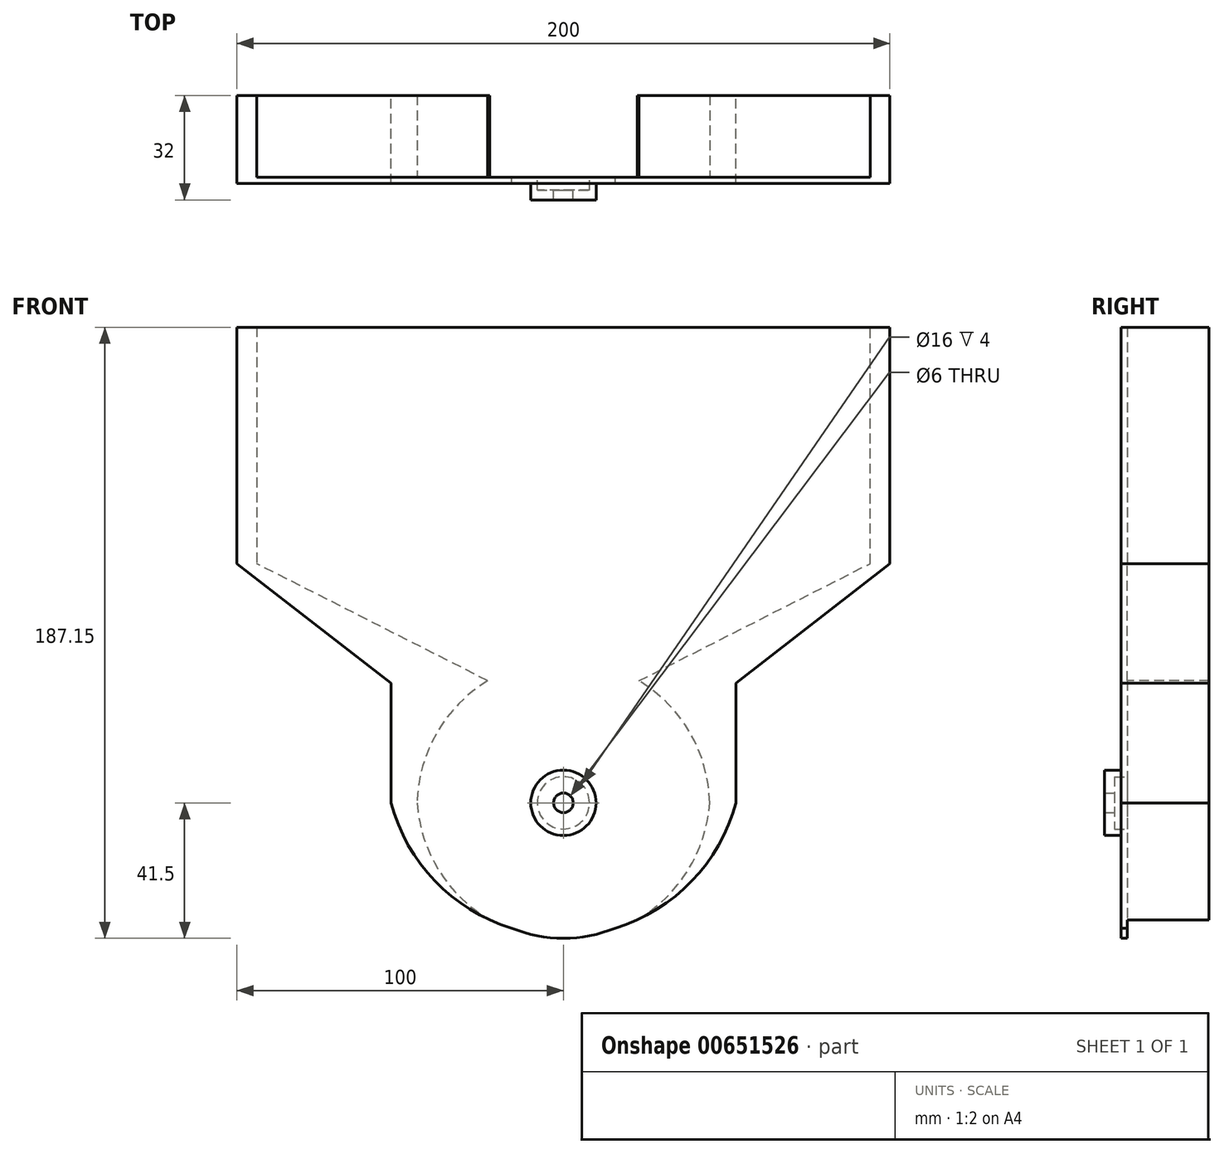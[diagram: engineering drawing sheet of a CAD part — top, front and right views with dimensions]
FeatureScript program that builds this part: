
annotation { "Feature Type Name" : "Feature", "Feature Type Description" : "" }
export const myFeature = defineFeature(function(context is Context, id is Id, definition is map)
    precondition{}
    {
        {
            var Q0;
            Q0=qCreatedBy(makeId("Front.planeOp"),FACE);
            var sketch = newSketch(context, id + "F0", { "sketchPlane" : qUnion([Q0])});
            skArc(sketch, "E0", {"start": v(15.88, -38.34) * mm, "mid": v(41.5, 0) * mm, "end": v(15.88, 38.34) * mm});
            skLineSegment(sketch, "E1", {"start": v(0, 0) * mm, "end": v(0, -41.5) * mm});
            skLineSegment(sketch, "E2", {"start": v(0, 0) * mm, "end": v(-15.88, -38.34) * mm});
            skLineSegment(sketch, "E3", {"start": v(0, 0) * mm, "end": v(15.88, -38.34) * mm});
            skArc(sketch, "E4", {"start": v(-15.88, -38.34) * mm, "mid": v(-39.33, -23.97) * mm, "end": v(-52.8, 0) * mm});
            skArc(sketch, "E5", {"start": v(15.88, -38.34) * mm, "mid": v(39.33, -23.97) * mm, "end": v(52.8, 0) * mm});
            skLineSegment(sketch, "E6", {"start": v(0, 0) * mm, "end": v(-15.88, 38.34) * mm});
            skLineSegment(sketch, "E7", {"start": v(0, 0) * mm, "end": v(15.88, 38.34) * mm});
            skArc(sketch, "E8.trimOffspring", {"start": v(-15.88, 38.34) * mm, "mid": v(-41.5, 0) * mm, "end": v(-15.88, -38.34) * mm});
            skArc(sketch, "E9", {"start": v(-15.88, -38.34) * mm, "mid": v(0, -41.5) * mm, "end": v(15.88, -38.34) * mm});
            skArc(sketch, "E10", {"start": v(-15.88, 38.34) * mm, "mid": v(0, 41.5) * mm, "end": v(15.88, 38.34) * mm});
            skLineSegment(sketch, "E11", {"start": v(-52.8, 0) * mm, "end": v(-52.8, 36.63) * mm});
            skLineSegment(sketch, "E12", {"start": v(-52.8, 36.63) * mm, "end": v(-100, 73.29) * mm});
            skLineSegment(sketch, "E13", {"start": v(-100, 73.29) * mm, "end": v(-100, 145.65) * mm});
            skLineSegment(sketch, "E14", {"start": v(0, 145.65) * mm, "end": v(-100, 145.65) * mm});
            skPoint(sketch, "E14.startSnap0", {"position": v(0, 41.5) * mm});
            skLineSegment(sketch, "E15", {"start": v(0, 145.65) * mm, "end": v(100, 145.65) * mm});
            skLineSegment(sketch, "E16", {"start": v(100, 145.65) * mm, "end": v(100, 73.29) * mm});
            skLineSegment(sketch, "E17", {"start": v(52.8, 0) * mm, "end": v(52.8, 36.63) * mm});
            skLineSegment(sketch, "E18", {"start": v(52.8, 36.63) * mm, "end": v(100, 73.29) * mm});
            skSolve(sketch);
        }
        {
            var Q0;
            Q0 = qSketchRegion(id + "F0", true);
            var Q1;
            Q1=makeQuery(id+"F0.imprint","IMPRINT",FACE,{"disambiguationData":[TD([[makeQuery(id+"F0.imprint","IMPRINT",EDGE,{"derivedFrom":sQuery(id+"F0.wireOp",EDGE,"E6")}),-1.0]])]});
            extrude(context, id + "F1", {"entities" : qUnion([Q0, Q1]), "depth" : 2 * mm, "offsetDistance" : 25 * mm});
        }
        {
            var Q0;
            Q0=makeQuery(id+"F1.opExtrude","CAP_FACE",FACE,{"disambiguationData":[OSD([sQuery(id+"F0.wireOp",EDGE,"E4"),sQuery(id+"F0.wireOp",EDGE,"E5"),sQuery(id+"F0.wireOp",EDGE,"E9"),sQuery(id+"F0.wireOp",EDGE,"E11"),sQuery(id+"F0.wireOp",EDGE,"E12"),sQuery(id+"F0.wireOp",EDGE,"E13"),sQuery(id+"F0.wireOp",EDGE,"E14"),sQuery(id+"F0.wireOp",EDGE,"E15"),sQuery(id+"F0.wireOp",EDGE,"E16"),sQuery(id+"F0.wireOp",EDGE,"E17"),sQuery(id+"F0.wireOp",EDGE,"E18")])],"isStart":false});
            var sketch = newSketch(context, id + "F2", { "sketchPlane" : qUnion([Q0])});
            skCircle(sketch, "E19", {"center": v(0, 0) * mm, "radius": 10 * mm});
            skSolve(sketch);
        }
        {
            var Q0;
            Q0=makeQuery(id+"F2.imprint","IMPRINT",FACE,{"disambiguationData":[TD([[makeQuery(id+"F2.imprint","IMPRINT",EDGE,{"derivedFrom":sQuery(id+"F2.wireOp",EDGE,"E19")}),1.0]])]});
            extrude(context, id + "F3", {"entities" : qUnion([Q0]), "operationType" : NewBodyOperationType.ADD, "depth" : 5 * mm, "offsetDistance" : 25 * mm});
        }
        {
            var Q0;
            Q0=makeQuery(id+"F1.opExtrude","CAP_FACE",FACE,{"disambiguationData":[OSD([sQuery(id+"F0.wireOp",EDGE,"E4"),sQuery(id+"F0.wireOp",EDGE,"E5"),sQuery(id+"F0.wireOp",EDGE,"E9"),sQuery(id+"F0.wireOp",EDGE,"E11"),sQuery(id+"F0.wireOp",EDGE,"E12"),sQuery(id+"F0.wireOp",EDGE,"E13"),sQuery(id+"F0.wireOp",EDGE,"E14"),sQuery(id+"F0.wireOp",EDGE,"E15"),sQuery(id+"F0.wireOp",EDGE,"E16"),sQuery(id+"F0.wireOp",EDGE,"E17"),sQuery(id+"F0.wireOp",EDGE,"E18")])],"isStart":true});
            var sketch = newSketch(context, id + "F4", { "sketchPlane" : qUnion([Q0])});
            skCircle(sketch, "E20", {"center": v(0, 0) * mm, "radius": 8 * mm});
            skSolve(sketch);
        }
        {
            var Q0;
            Q0=makeQuery(id+"F4.imprint","IMPRINT",FACE,{"disambiguationData":[TD([[makeQuery(id+"F4.imprint","IMPRINT",EDGE,{"derivedFrom":sQuery(id+"F4.wireOp",EDGE,"E20")}),1.0]])]});
            extrude(context, id + "F5", {"entities" : qUnion([Q0]), "operationType" : NewBodyOperationType.REMOVE, "oppositeDirection" : true, "depth" : 4 * mm, "offsetDistance" : 25 * mm});
        }
        {
            var Q0;
            Q0=makeQuery(id+"F1.opExtrude","CAP_FACE",FACE,{"disambiguationData":[OSD([sQuery(id+"F0.wireOp",EDGE,"E4"),sQuery(id+"F0.wireOp",EDGE,"E5"),sQuery(id+"F0.wireOp",EDGE,"E9"),sQuery(id+"F0.wireOp",EDGE,"E11"),sQuery(id+"F0.wireOp",EDGE,"E12"),sQuery(id+"F0.wireOp",EDGE,"E13"),sQuery(id+"F0.wireOp",EDGE,"E14"),sQuery(id+"F0.wireOp",EDGE,"E15"),sQuery(id+"F0.wireOp",EDGE,"E16"),sQuery(id+"F0.wireOp",EDGE,"E17"),sQuery(id+"F0.wireOp",EDGE,"E18")])],"isStart":true});
            var sketch = newSketch(context, id + "F6", { "sketchPlane" : qUnion([Q0])});
            skCircle(sketch, "E21", {"center": v(0, 0) * mm, "radius": 3 * mm});
            skSolve(sketch);
        }
        {
            var Q0;
            Q0 = qSketchRegion(id + "F6", true);
            extrude(context, id + "F7", {"entities" : qUnion([Q0]), "operationType" : NewBodyOperationType.REMOVE, "oppositeDirection" : true, "depth" : 25 * mm, "offsetDistance" : 25 * mm});
        }
        {
            var Q0;
            Q0=makeQuery(id+"F0.imprint","IMPRINT",FACE,{"disambiguationData":[TD([[makeQuery(id+"F0.imprint","IMPRINT",EDGE,{"derivedFrom":sQuery(id+"F0.wireOp",EDGE,"E0")}),-1.0]])]});
            var sketch = newSketch(context, id + "F8", { "sketchPlane" : qUnion([Q0])});
            skPoint(sketch, "E22.0", {"position": v(-50, 145.65) * mm});
            skLineSegment(sketch, "E23.0", {"start": v(-100, 73.29) * mm, "end": v(-100, 145.65) * mm});
            skLineSegment(sketch, "E24.0", {"start": v(-52.8, 36.63) * mm, "end": v(-100, 73.29) * mm});
            skLineSegment(sketch, "E25.0", {"start": v(52.8, 36.63) * mm, "end": v(100, 73.29) * mm});
            skLineSegment(sketch, "E26.0", {"start": v(-52.8, 0) * mm, "end": v(-52.8, 36.63) * mm});
            skLineSegment(sketch, "E27.0", {"start": v(52.8, 0) * mm, "end": v(52.8, 36.63) * mm});
            skLineSegment(sketch, "E28.0", {"start": v(100, 145.65) * mm, "end": v(100, 73.29) * mm});
            skArc(sketch, "E29", {"start": v(24.35, -34.97) * mm, "mid": v(38.75, -19.92) * mm, "end": v(44.8, 0) * mm});
            skArc(sketch, "E30", {"start": v(44.8, 0) * mm, "mid": v(38.79, 21.47) * mm, "end": v(23.17, 37.39) * mm});
            skLineSegment(sketch, "E31", {"start": v(23.17, 37.39) * mm, "end": v(94, 73.29) * mm});
            skLineSegment(sketch, "E32", {"start": v(94, 73.29) * mm, "end": v(94, 145.65) * mm});
            skLineSegment(sketch, "E33.MirrorCS", {"start": v(-94, 73.29) * mm, "end": v(-94, 143.97) * mm});
            skLineSegment(sketch, "E34.MirrorCS", {"start": v(-23.17, 37.39) * mm, "end": v(-94, 73.29) * mm});
            skArc(sketch, "E35.MirrorCS", {"start": v(-44.8, 0) * mm, "mid": v(-38.79, 21.47) * mm, "end": v(-23.17, 37.39) * mm});
            skArc(sketch, "E36", {"start": v(52.8, 0) * mm, "mid": v(42.36, -20.56) * mm, "end": v(24.35, -34.97) * mm});
            skLineSegment(sketch, "E37", {"start": v(52.8, 0) * mm, "end": v(44.8, 0) * mm});
            skLineSegment(sketch, "E38", {"start": v(100, 145.65) * mm, "end": v(94, 145.65) * mm});
            skLineSegment(sketch, "E39", {"start": v(-100, 145.65) * mm, "end": v(-94, 145.65) * mm});
            skLineSegment(sketch, "E40", {"start": v(-94, 145.65) * mm, "end": v(-94, 143.97) * mm});
            skLineSegment(sketch, "E41", {"start": v(-44.8, 0) * mm, "end": v(-52.8, 0) * mm});
            skSolve(sketch);
        }
        {
            var Q0;
            Q0=makeQuery(id+"F8.imprint","IMPRINT",FACE,{"disambiguationData":[TD([[makeQuery(id+"F8.imprint","IMPRINT",EDGE,{"derivedFrom":sQuery(id+"F8.wireOp",EDGE,"eec11fa1-e937-4813-9ca2-695186ab6096.0")}),-1.0]])]});
            var Q1;
            Q1=makeQuery(id+"F8.imprint","IMPRINT",FACE,{"disambiguationData":[TD([[makeQuery(id+"F8.imprint","IMPRINT",EDGE,{"derivedFrom":sQuery(id+"F8.wireOp",EDGE,"E25.0")}),1.0]])]});
            var Q2;
            Q2=makeQuery(id+"F8.imprint","IMPRINT",FACE,{"disambiguationData":[TD([[makeQuery(id+"F8.imprint","IMPRINT",EDGE,{"derivedFrom":sQuery(id+"F8.wireOp",EDGE,"E23.0")}),-1.0]])]});
            extrude(context, id + "F9", {"entities" : qUnion([Q0, Q1, Q2]), "operationType" : NewBodyOperationType.ADD, "oppositeDirection" : true, "depth" : 25 * mm, "offsetDistance" : 25 * mm});
        }
        {
            var Q0;
            Q0=makeQuery(id+"F0.imprint","IMPRINT",FACE,{"disambiguationData":[TD([[makeQuery(id+"F0.imprint","IMPRINT",EDGE,{"derivedFrom":sQuery(id+"F0.wireOp",EDGE,"E0")}),-1.0]])]});
            var sketch = newSketch(context, id + "F10", { "sketchPlane" : qUnion([Q0])});
            skArc(sketch, "E42.0", {"start": v(15.88, -38.34) * mm, "mid": v(39.33, -23.97) * mm, "end": v(52.8, 0) * mm});
            skArc(sketch, "E43.0", {"start": v(-15.88, -38.34) * mm, "mid": v(-39.33, -23.97) * mm, "end": v(-52.8, 0) * mm});
            skPoint(sketch, "E44.0", {"position": v(48.8, 0) * mm});
            skPoint(sketch, "E45.0", {"position": v(44.8, 0) * mm});
            skLineSegment(sketch, "E46", {"start": v(52.8, 0) * mm, "end": v(44.8, 0) * mm});
            skCircle(sketch, "E47.0", {"center": v(0, 0) * mm, "radius": 3 * mm});
            skArc(sketch, "E48", {"start": v(44.8, 0) * mm, "mid": v(38.15, -20.68) * mm, "end": v(22.57, -35.82) * mm});
            skLineSegment(sketch, "E49", {"start": v(0, 3) * mm, "end": v(0, -3) * mm});
            skArc(sketch, "E50.MirrorCS", {"start": v(-44.8, 0) * mm, "mid": v(-38.15, -20.68) * mm, "end": v(-22.57, -35.82) * mm});
            skLineSegment(sketch, "E51.MirrorCS", {"start": v(-52.8, 0) * mm, "end": v(-44.8, 0) * mm});
            skSolve(sketch);
        }
        {
            var Q0;
            {var subQ0=sQuery(id+"F10.wireOp",EDGE,"E46");Q0=makeQuery(id+"F10.imprint","IMPRINT",FACE,{"disambiguationData":[TD([[makeQuery(id+"F10.imprint","IMPRINT",EDGE,{"derivedFrom":subQ0}),1.0]])]});}
            var Q1;
            Q1=sQuery(id+"F10.wireOp",EDGE,"E48");
            var Q2;
            Q2=sQuery(id+"F10.wireOp",EDGE,"E46");
            var Q3;
            Q3=sQuery(id+"F0.wireOp",EDGE,"E5");
            extrude(context, id + "F11", {"entities" : qUnion([Q0]), "operationType" : NewBodyOperationType.ADD, "surfaceEntities" : qUnion([Q1, Q2, Q3]), "oppositeDirection" : true, "depth" : 25 * mm, "offsetDistance" : 25 * mm});
        }
        {
            var Q0;
            {var subQ0=sQuery(id+"F10.wireOp",EDGE,"E50.MirrorCS");Q0=makeQuery(id+"F10.imprint","IMPRINT",FACE,{"disambiguationData":[TD([[makeQuery(id+"F10.imprint","IMPRINT",EDGE,{"derivedFrom":subQ0}),-1.0]])]});}
            extrude(context, id + "F12", {"entities" : qUnion([Q0]), "operationType" : NewBodyOperationType.ADD, "oppositeDirection" : true, "depth" : 25 * mm, "offsetDistance" : 25 * mm});
        }
    });
